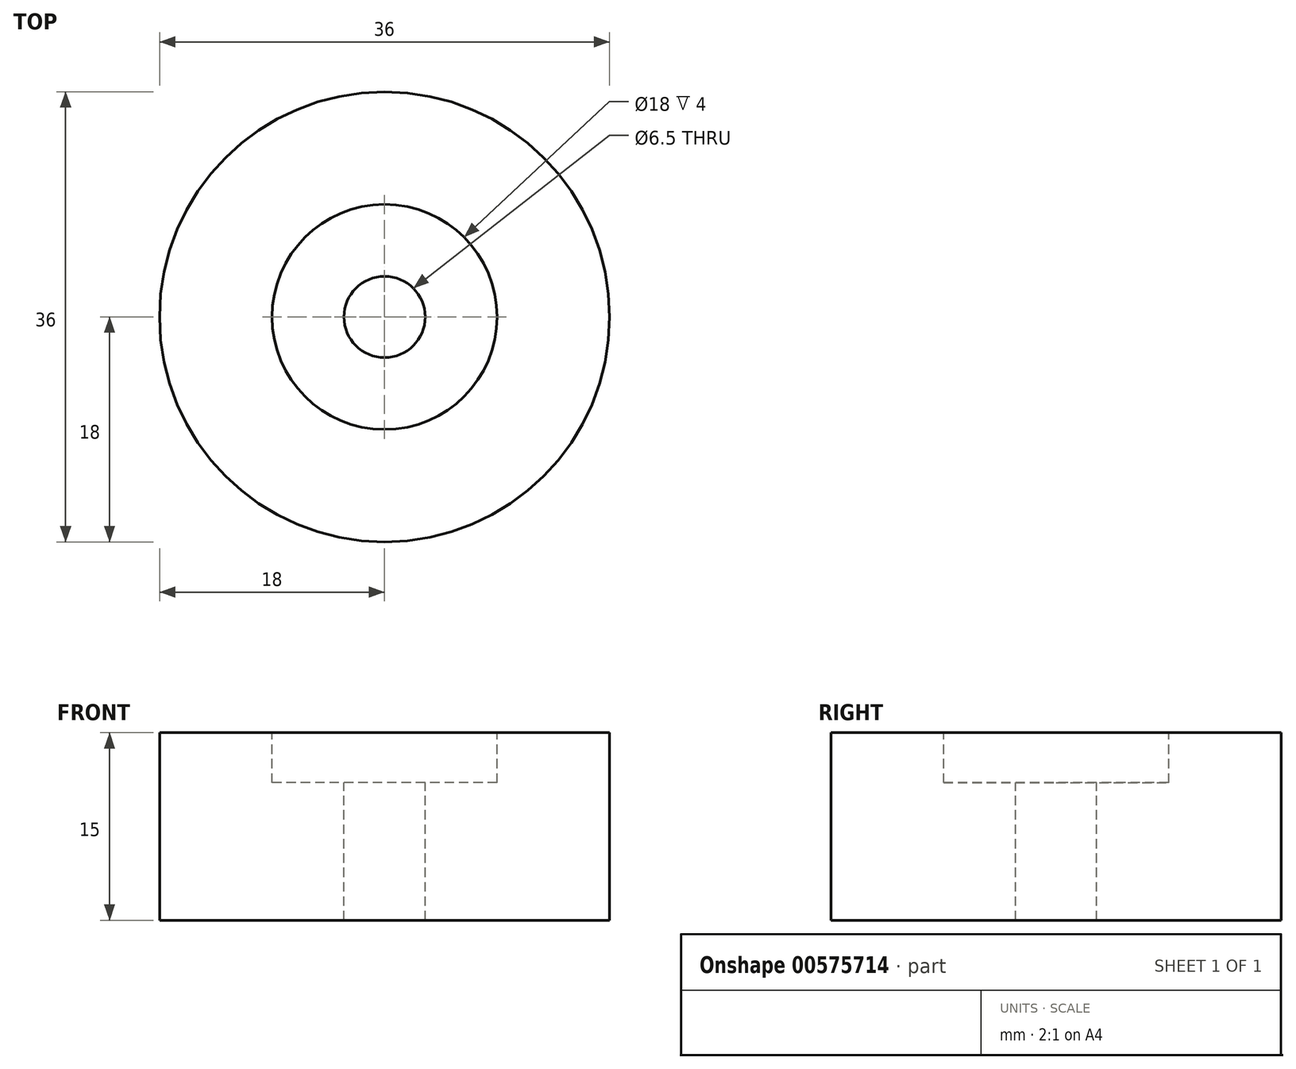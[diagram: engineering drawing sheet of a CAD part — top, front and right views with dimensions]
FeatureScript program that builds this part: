
annotation { "Feature Type Name" : "Feature", "Feature Type Description" : "" }
export const myFeature = defineFeature(function(context is Context, id is Id, definition is map)
    precondition{}
    {
        {
            var Q0;
            Q0=qCreatedBy(makeId("Top.planeOp"),FACE);
            var sketch = newSketch(context, id + "F0", { "sketchPlane" : qUnion([Q0])});
            skCircle(sketch, "E0", {"center": v(0, 0) * mm, "radius": 18 * mm});
            skSolve(sketch);
        }
        {
            var Q0;
            Q0=makeQuery(id+"F0.imprint","IMPRINT",FACE,{"disambiguationData":[TD([[makeQuery(id+"F0.imprint","IMPRINT",EDGE,{"derivedFrom":sQuery(id+"F0.wireOp",EDGE,"E0")}),1.0]])]});
            extrude(context, id + "F1", {"entities" : qUnion([Q0]), "depth" : 15 * mm, "offsetDistance" : 25 * mm});
        }
        {
            var Q0;
            Q0=makeQuery(id+"F1.opExtrude","CAP_FACE",FACE,{"disambiguationData":[OSD([sQuery(id+"F0.wireOp",EDGE,"E0")])],"isStart":false});
            var sketch = newSketch(context, id + "F2", { "sketchPlane" : qUnion([Q0])});
            skCircle(sketch, "E1", {"center": v(0, 0) * mm, "radius": 9 * mm});
            skCircle(sketch, "E2", {"center": v(0, 0) * mm, "radius": 3.25 * mm});
            skSolve(sketch);
        }
        {
            var Q0;
            Q0=makeQuery(id+"F2.imprint","IMPRINT",FACE,{"disambiguationData":[TD([[makeQuery(id+"F2.imprint","IMPRINT",EDGE,{"derivedFrom":sQuery(id+"F2.wireOp",EDGE,"E1")}),1.0]])]});
            var Q1;
            Q1=sQuery(id+"F2.wireOp",EDGE,"E1");
            extrude(context, id + "F3", {"entities" : qUnion([Q0]), "operationType" : NewBodyOperationType.REMOVE, "surfaceEntities" : qUnion([Q1]), "oppositeDirection" : true, "depth" : 4 * mm, "offsetDistance" : 25 * mm});
        }
        {
            var Q0;
            Q0=makeQuery(id+"F2.imprint","IMPRINT",FACE,{"disambiguationData":[TD([[makeQuery(id+"F2.imprint","IMPRINT",EDGE,{"derivedFrom":sQuery(id+"F2.wireOp",EDGE,"E2")}),1.0]])]});
            extrude(context, id + "F4", {"entities" : qUnion([Q0]), "operationType" : NewBodyOperationType.REMOVE, "oppositeDirection" : true, "depth" : 25 * mm, "offsetDistance" : 25 * mm});
        }
    });
